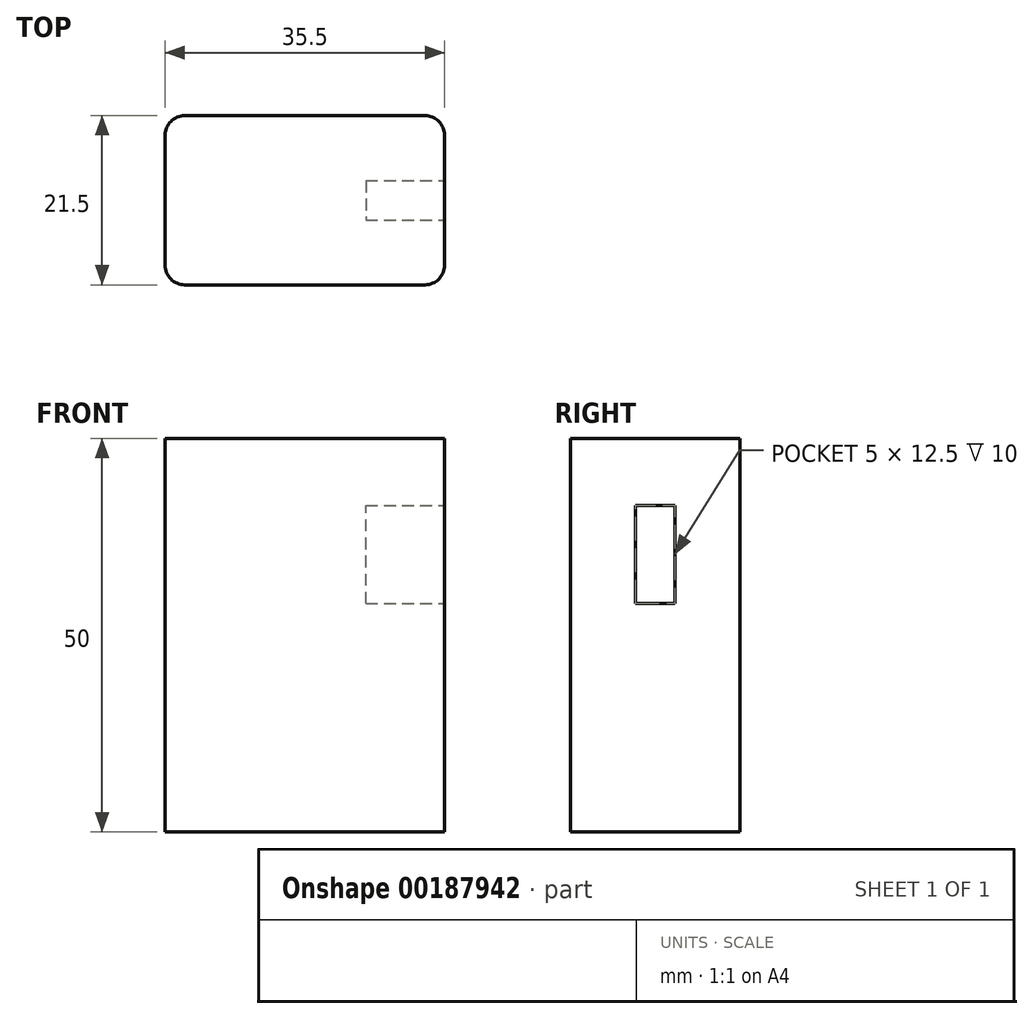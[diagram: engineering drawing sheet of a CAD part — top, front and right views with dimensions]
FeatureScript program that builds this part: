
annotation { "Feature Type Name" : "Feature", "Feature Type Description" : "" }
export const myFeature = defineFeature(function(context is Context, id is Id, definition is map)
    precondition{}
    {
        {
            var Q0;
            Q0=qCreatedBy(makeId("Top.planeOp"),FACE);
            var sketch = newSketch(context, id + "F0", { "sketchPlane" : qUnion([Q0])});
            skLineSegment(sketch, "E0.bottom", {"start": v(15.25, -10.75) * mm, "end": v(-15.25, -10.75) * mm});
            skLineSegment(sketch, "E0.top", {"start": v(15.25, 10.75) * mm, "end": v(-15.25, 10.75) * mm});
            skLineSegment(sketch, "E0.left", {"start": v(17.75, -8.25) * mm, "end": v(17.75, 8.25) * mm});
            skLineSegment(sketch, "E0.right", {"start": v(-17.75, -8.25) * mm, "end": v(-17.75, 8.25) * mm});
            skPoint(sketch, "E0.middle", {"position": v(0, 0) * mm});
            skPoint(sketch, "E1.visualSharp", {"position": v(17.75, 10.75) * mm});
            skArc(sketch, "E1.filletArc", {"start": v(17.75, 8.25) * mm, "mid": v(17.02, 10.02) * mm, "end": v(15.25, 10.75) * mm});
            skPoint(sketch, "E2.visualSharp", {"position": v(17.75, -10.75) * mm});
            skArc(sketch, "E2.filletArc", {"start": v(15.25, -10.75) * mm, "mid": v(17.02, -10.02) * mm, "end": v(17.75, -8.25) * mm});
            skPoint(sketch, "E3.visualSharp", {"position": v(-17.75, -10.75) * mm});
            skArc(sketch, "E3.filletArc", {"start": v(-17.75, -8.25) * mm, "mid": v(-17.02, -10.02) * mm, "end": v(-15.25, -10.75) * mm});
            skPoint(sketch, "E4.visualSharp", {"position": v(-17.75, 10.75) * mm});
            skArc(sketch, "E4.filletArc", {"start": v(-15.25, 10.75) * mm, "mid": v(-17.02, 10.02) * mm, "end": v(-17.75, 8.25) * mm});
            skSolve(sketch);
        }
        {
            var Q0;
            Q0 = qSketchRegion(id + "F0", true);
            extrude(context, id + "F1", {"entities" : qUnion([Q0]), "depth" : 50 * mm});
        }
        {
            var Q0;
            Q0=makeQuery(id+"F1.opExtrude","SWEPT_FACE",FACE,{"disambiguationData":[OSD([sQuery(id+"F0.wireOp",EDGE,"E0.left")])]});
            var sketch = newSketch(context, id + "F2", { "sketchPlane" : qUnion([Q0])});
            skLineSegment(sketch, "E5.bottom", {"start": v(2.5, 29) * mm, "end": v(-2.5, 29) * mm});
            skLineSegment(sketch, "E5.top", {"start": v(2.5, 41.5) * mm, "end": v(-2.5, 41.5) * mm});
            skLineSegment(sketch, "E5.left", {"start": v(2.5, 29) * mm, "end": v(2.5, 41.5) * mm});
            skLineSegment(sketch, "E5.right", {"start": v(-2.5, 29) * mm, "end": v(-2.5, 41.5) * mm});
            skPoint(sketch, "E5.middle", {"position": v(0, 35.25) * mm});
            skSolve(sketch);
        }
        {
            var Q0;
            Q0 = qSketchRegion(id + "F2", true);
            extrude(context, id + "F3", {"entities" : qUnion([Q0]), "operationType" : NewBodyOperationType.REMOVE, "oppositeDirection" : true, "depth" : 10 * mm});
        }
    });
